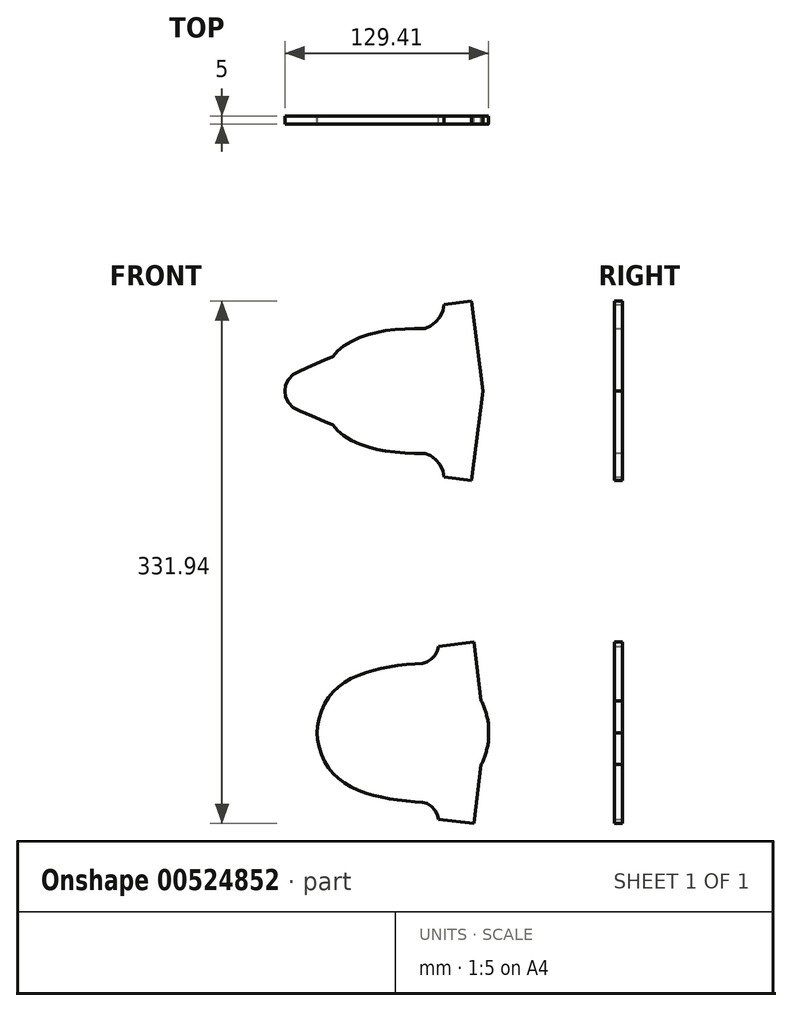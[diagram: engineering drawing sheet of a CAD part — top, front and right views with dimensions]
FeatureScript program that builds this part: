
annotation { "Feature Type Name" : "Feature", "Feature Type Description" : "" }
export const myFeature = defineFeature(function(context is Context, id is Id, definition is map)
    precondition{}
    {
        {
            var Q0;
            Q0=qCreatedBy(makeId("Front.planeOp"),FACE);
            var sketch = newSketch(context, id + "F0", { "sketchPlane" : qUnion([Q0])});
            skLineSegment(sketch, "E0", {"start": v(262.47, -863.76) * mm, "end": v(399.25, -863.76) * mm, "construction": true});
            skFitSpline(sketch, "E1", {"points": [v(276.55, -863.76) * mm, v(276.61, -866.83) * mm, v(277.12, -870.25) * mm, v(278.26, -875.06) * mm, v(280.03, -879.61) * mm, v(282, -883.4) * mm, v(284.27, -886.76) * mm, v(286.6, -889.54) * mm, v(289.58, -892.45) * mm, v(292.43, -894.8) * mm, v(296.23, -897.26) * mm, v(299.7, -898.97) * mm, v(305.08, -901.19) * mm, v(309.38, -902.64) * mm, v(312.93, -903.65) * mm, v(317.6, -904.8) * mm, v(322.92, -905.8) * mm, v(327.67, -906.5) * mm, v(333.55, -907.2) * mm, v(339.18, -907.57) * mm, v(343.42, -907.83) * mm, v(344.37, -908.08) * mm, v(345.95, -908.71) * mm, v(347.91, -909.85) * mm, v(349.37, -911.05) * mm, v(350.7, -912.38) * mm, v(351.9, -914.03) * mm, v(352.79, -915.99) * mm, v(353.3, -917.38) * mm, v(353.48, -918.65) * mm], "startDerivative": vector(-0.77, -94.38) * mm, "endDerivative": vector(6.05, -60.76) * mm});
            skLineSegment(sketch, "E2", {"start": v(353.48, -918.65) * mm, "end": v(376.07, -921.43) * mm});
            skLineSegment(sketch, "E3", {"start": v(376.07, -921.43) * mm, "end": v(380.68, -883.97) * mm});
            skFitSpline(sketch, "E4", {"points": [v(380.68, -883.97) * mm, v(381.38, -882.77) * mm, v(382.14, -880.94) * mm, v(382.9, -878.85) * mm, v(383.66, -876.7) * mm, v(384.23, -874.49) * mm, v(384.8, -872.08) * mm, v(385.18, -869.68) * mm, v(385.37, -867.53) * mm, v(385.43, -865.5) * mm, v(385.43, -863.76) * mm], "startDerivative": vector(8.72, 13.74) * mm, "endDerivative": vector(-0.1, 18.68) * mm});
            skFitSpline(sketch, "E5.MirrorCS", {"points": [v(276.55, -863.76) * mm, v(276.61, -860.7) * mm, v(277.12, -857.28) * mm, v(278.26, -852.47) * mm, v(280.03, -847.92) * mm, v(282, -844.12) * mm, v(284.27, -840.77) * mm, v(286.6, -837.98) * mm, v(289.58, -835.07) * mm, v(292.43, -832.73) * mm, v(296.23, -830.26) * mm, v(299.7, -828.56) * mm, v(305.08, -826.34) * mm, v(309.38, -824.89) * mm, v(312.93, -823.87) * mm, v(317.6, -822.74) * mm, v(322.92, -821.72) * mm, v(327.67, -821.03) * mm, v(333.55, -820.33) * mm, v(339.18, -819.95) * mm, v(343.42, -819.7) * mm, v(344.37, -819.45) * mm, v(345.95, -818.81) * mm, v(347.91, -817.67) * mm, v(349.37, -816.47) * mm, v(350.7, -815.14) * mm, v(351.9, -813.5) * mm, v(352.79, -811.54) * mm, v(353.3, -810.15) * mm, v(353.48, -808.88) * mm], "startDerivative": vector(-0.77, 94.38) * mm, "endDerivative": vector(6.05, 60.76) * mm});
            skLineSegment(sketch, "E6.MirrorCS", {"start": v(353.48, -808.88) * mm, "end": v(376.07, -806.1) * mm});
            skLineSegment(sketch, "E7.MirrorCS", {"start": v(376.07, -806.1) * mm, "end": v(380.68, -843.56) * mm});
            skFitSpline(sketch, "E8.MirrorCS", {"points": [v(380.68, -843.56) * mm, v(381.38, -844.75) * mm, v(382.14, -846.59) * mm, v(382.9, -848.67) * mm, v(383.66, -850.83) * mm, v(384.23, -853.04) * mm, v(384.8, -855.44) * mm, v(385.18, -857.85) * mm, v(385.37, -860) * mm, v(385.43, -862.02) * mm, v(385.43, -863.76) * mm], "startDerivative": vector(8.72, -13.74) * mm, "endDerivative": vector(-0.1, -18.68) * mm});
            skLineSegment(sketch, "E9", {"start": v(336.22, -914.54) * mm, "end": v(336.22, -816.29) * mm, "construction": true});
            skSolve(sketch);
        }
        {
            var Q0;
            Q0=qCreatedBy(makeId("Front.planeOp"),FACE);
            var sketch = newSketch(context, id + "F1", { "sketchPlane" : qUnion([Q0])});
            skLineSegment(sketch, "E10", {"start": v(251.85, -646.58) * mm, "end": v(392.16, -646.58) * mm, "construction": true});
            skLineSegment(sketch, "E11", {"start": v(381.69, -646.58) * mm, "end": v(374.5, -703.67) * mm});
            skLineSegment(sketch, "E12", {"start": v(374.5, -703.67) * mm, "end": v(356.89, -701.46) * mm});
            skFitSpline(sketch, "E13", {"points": [v(356.89, -701.46) * mm, v(356.83, -700) * mm, v(356.26, -697.34) * mm, v(355.36, -694.97) * mm, v(354, -692.67) * mm, v(352.65, -691.05) * mm, v(350.92, -689.47) * mm, v(349.04, -688.12) * mm, v(347.42, -687.25) * mm, v(345.4, -686.35) * mm, v(344.71, -686.28) * mm, v(338.28, -686.24) * mm, v(333.5, -686.09) * mm, v(328.17, -685.65) * mm, v(323.59, -685.3) * mm, v(318.7, -684.62) * mm, v(314.76, -683.84) * mm, v(311.1, -682.96) * mm, v(307.24, -681.8) * mm, v(302.95, -680.13) * mm, v(299.2, -678.48) * mm, v(295.15, -676.23) * mm, v(292.17, -674.13) * mm, v(289.63, -671.94) * mm, v(287, -669.06) * mm, v(286.41, -668.33) * mm, v(285.73, -667.99) * mm, v(278.46, -664.86) * mm, v(270.5, -661.35) * mm, v(263.34, -658.23) * mm, v(261.48, -657.25) * mm, v(259.78, -655.7) * mm, v(258.26, -653.84) * mm, v(257.22, -652.18) * mm, v(256.5, -650.39) * mm, v(256.09, -648.47) * mm, v(256.02, -646.58) * mm], "startDerivative": vector(0.22, 70.52) * mm, "endDerivative": vector(-7.34, 85.12) * mm});
            skLineSegment(sketch, "E14.MirrorCS", {"start": v(381.69, -646.58) * mm, "end": v(374.5, -589.5) * mm});
            skLineSegment(sketch, "E15.MirrorCS", {"start": v(374.5, -589.5) * mm, "end": v(356.89, -591.71) * mm});
            skFitSpline(sketch, "E16.MirrorCS", {"points": [v(356.89, -591.71) * mm, v(356.83, -593.16) * mm, v(356.26, -595.83) * mm, v(355.36, -598.2) * mm, v(354, -600.5) * mm, v(352.65, -602.11) * mm, v(350.92, -603.7) * mm, v(349.04, -605.05) * mm, v(347.42, -605.91) * mm, v(345.4, -606.81) * mm, v(344.71, -606.89) * mm, v(338.28, -606.93) * mm, v(333.5, -607.08) * mm, v(328.17, -607.52) * mm, v(323.59, -607.86) * mm, v(318.7, -608.54) * mm, v(314.76, -609.32) * mm, v(311.1, -610.2) * mm, v(307.24, -611.37) * mm, v(302.95, -613.03) * mm, v(299.2, -614.7) * mm, v(295.15, -616.93) * mm, v(292.17, -619.03) * mm, v(289.63, -621.23) * mm, v(287, -624.1) * mm, v(286.41, -624.84) * mm, v(285.73, -625.18) * mm, v(278.46, -628.3) * mm, v(270.5, -631.81) * mm, v(263.34, -634.94) * mm, v(261.48, -635.91) * mm, v(259.78, -637.47) * mm, v(258.26, -639.33) * mm, v(257.22, -640.98) * mm, v(256.5, -642.78) * mm, v(256.09, -644.7) * mm, v(256.02, -646.58) * mm], "startDerivative": vector(0.22, -70.52) * mm, "endDerivative": vector(-7.34, -85.12) * mm});
            skLineSegment(sketch, "E17", {"start": v(336.75, -693.58) * mm, "end": v(336.75, -601.12) * mm, "construction": true});
            skSolve(sketch);
        }
        {
            var Q0;
            Q0 = qSketchRegion(id + "F0", true);
            extrude(context, id + "F2", {"entities" : qUnion([Q0]), "endBound" : BoundingType.SYMMETRIC, "depth" : 5 * mm, "offsetDistance" : 25 * mm});
        }
        {
            var Q0;
            Q0 = qSketchRegion(id + "F1", true);
            extrude(context, id + "F3", {"entities" : qUnion([Q0]), "endBound" : BoundingType.SYMMETRIC, "depth" : 5 * mm, "offsetDistance" : 25 * mm});
        }
    });
